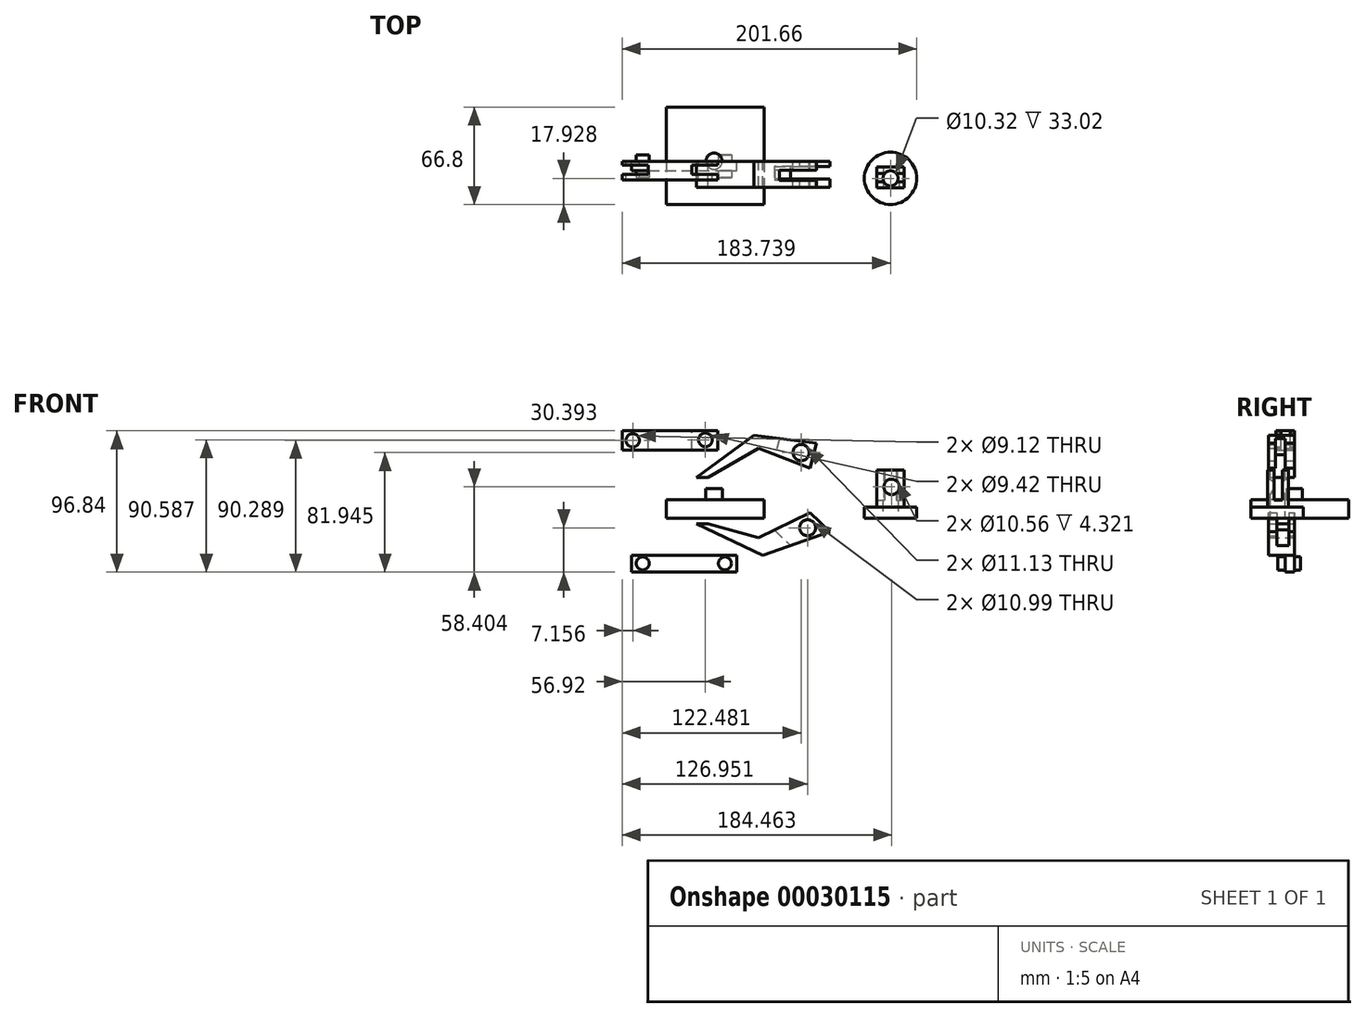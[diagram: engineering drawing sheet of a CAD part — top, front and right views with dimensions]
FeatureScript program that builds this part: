
annotation { "Feature Type Name" : "Feature", "Feature Type Description" : "" }
export const myFeature = defineFeature(function(context is Context, id is Id, definition is map)
    precondition{}
    {
        {
            var Q0;
            Q0=qCreatedBy(makeId("Top.planeOp"),FACE);
            var sketch = newSketch(context, id + "F0", { "sketchPlane" : qUnion([Q0])});
            skLineSegment(sketch, "E0.bottom", {"start": v(-32.78, 37.1) * mm, "end": v(34.27, 37.1) * mm});
            skLineSegment(sketch, "E0.top", {"start": v(-32.78, -29.65) * mm, "end": v(34.27, -29.65) * mm});
            skLineSegment(sketch, "E0.left", {"start": v(-32.78, 37.1) * mm, "end": v(-32.78, -29.65) * mm});
            skLineSegment(sketch, "E0.right", {"start": v(34.27, 37.1) * mm, "end": v(34.27, -29.65) * mm});
            skSolve(sketch);
        }
        {
            var Q0;
            Q0=makeQuery(id+"F0.imprint","IMPRINT",FACE,{"disambiguationData":[TD([[makeQuery(id+"F0.imprint","IMPRINT",EDGE,{"derivedFrom":sQuery(id+"F0.wireOp",EDGE,"E0.bottom")}),-1.0]])]});
            extrude(context, id + "F1", {"entities" : qUnion([Q0]), "depth" : 12.7 * mm});
        }
        {
            var Q0;
            Q0=qCreatedBy(makeId("Front.planeOp"),FACE);
            var sketch = newSketch(context, id + "F2", { "sketchPlane" : qUnion([Q0])});
            skLineSegment(sketch, "E1.bottom", {"start": v(-62.88, 60.04) * mm, "end": v(2.68, 60.04) * mm});
            skLineSegment(sketch, "E1.top", {"start": v(-62.88, 46.93) * mm, "end": v(2.68, 46.93) * mm});
            skLineSegment(sketch, "E1.left", {"start": v(-62.88, 60.04) * mm, "end": v(-62.88, 46.93) * mm});
            skLineSegment(sketch, "E1.right", {"start": v(2.68, 60.04) * mm, "end": v(2.68, 46.93) * mm});
            skCircle(sketch, "E2", {"center": v(-55.72, 53.49) * mm, "radius": 4.56 * mm});
            skCircle(sketch, "E3", {"center": v(-5.96, 53.79) * mm, "radius": 4.71 * mm});
            skSolve(sketch);
        }
        {
            var Q0;
            Q0=makeQuery(id+"F2.imprint","IMPRINT",FACE,{"disambiguationData":[TD([[makeQuery(id+"F2.imprint","IMPRINT",EDGE,{"derivedFrom":sQuery(id+"F2.wireOp",EDGE,"E1.bottom")}),-1.0]])]});
            extrude(context, id + "F3", {"entities" : qUnion([Q0]), "depth" : 12.7 * mm});
        }
        {
            var Q0;
            Q0=makeQuery(id+"F3.opExtrude","SWEPT_FACE",FACE,{"disambiguationData":[OSD([sQuery(id+"F2.wireOp",EDGE,"E1.bottom")])]});
            var sketch = newSketch(context, id + "F4", { "sketchPlane" : qUnion([Q0])});
            skLineSegment(sketch, "E4.bottom", {"start": v(-62.88, -2.83) * mm, "end": v(-45.1, -2.83) * mm});
            skLineSegment(sketch, "E4.top", {"start": v(-62.88, -9.18) * mm, "end": v(-45.1, -9.18) * mm});
            skLineSegment(sketch, "E4.left", {"start": v(-62.88, -2.83) * mm, "end": v(-62.88, -9.18) * mm});
            skLineSegment(sketch, "E4.right", {"start": v(-45.1, -2.83) * mm, "end": v(-45.1, -9.18) * mm});
            skLineSegment(sketch, "E5.bottom", {"start": v(-15.1, -9.18) * mm, "end": v(2.68, -9.18) * mm});
            skLineSegment(sketch, "E5.top", {"start": v(-15.1, -2.83) * mm, "end": v(2.68, -2.83) * mm});
            skLineSegment(sketch, "E5.left", {"start": v(-15.1, -9.18) * mm, "end": v(-15.1, -2.83) * mm});
            skLineSegment(sketch, "E5.right", {"start": v(2.68, -9.18) * mm, "end": v(2.68, -2.83) * mm});
            skSolve(sketch);
        }
        {
            var Q0;
            Q0=makeQuery(id+"F4.imprint","IMPRINT",FACE,{"disambiguationData":[TD([[makeQuery(id+"F4.imprint","IMPRINT",EDGE,{"derivedFrom":sQuery(id+"F4.wireOp",EDGE,"E4.bottom")}),-1.0]])]});
            var Q1;
            Q1=makeQuery(id+"F4.imprint","IMPRINT",FACE,{"disambiguationData":[TD([[makeQuery(id+"F4.imprint","IMPRINT",EDGE,{"derivedFrom":sQuery(id+"F4.wireOp",EDGE,"E5.bottom")}),1.0]])]});
            extrude(context, id + "F5", {"entities" : qUnion([Q0, Q1]), "operationType" : NewBodyOperationType.REMOVE, "oppositeDirection" : true, "depth" : 25.4 * mm});
        }
        {
            var Q0;
            Q0=qCreatedBy(makeId("Front.planeOp"),FACE);
            var sketch = newSketch(context, id + "F6", { "sketchPlane" : qUnion([Q0])});
            skLineSegment(sketch, "E6.bottom", {"start": v(-56.62, -25.18) * mm, "end": v(15.5, -25.18) * mm});
            skLineSegment(sketch, "E6.top", {"start": v(-56.62, -36.8) * mm, "end": v(15.5, -36.8) * mm});
            skLineSegment(sketch, "E6.left", {"start": v(-56.62, -25.18) * mm, "end": v(-56.62, -36.8) * mm});
            skLineSegment(sketch, "E6.right", {"start": v(15.5, -25.18) * mm, "end": v(15.5, -36.8) * mm});
            skSolve(sketch);
        }
        {
            var Q0;
            Q0=makeQuery(id+"F6.imprint","IMPRINT",FACE,{"disambiguationData":[TD([[makeQuery(id+"F6.imprint","IMPRINT",EDGE,{"derivedFrom":sQuery(id+"F6.wireOp",EDGE,"E6.bottom")}),-1.0]])]});
            extrude(context, id + "F7", {"entities" : qUnion([Q0]), "depth" : 6.35 * mm});
        }
        {
            var Q0;
            Q0=makeQuery(id+"F7.opExtrude","CAP_FACE",FACE,{"disambiguationData":[OSD([sQuery(id+"F6.wireOp",EDGE,"E6.bottom"),sQuery(id+"F6.wireOp",EDGE,"E6.top"),sQuery(id+"F6.wireOp",EDGE,"E6.left"),sQuery(id+"F6.wireOp",EDGE,"E6.right")])],"isStart":false});
            var sketch = newSketch(context, id + "F8", { "sketchPlane" : qUnion([Q0])});
            skCircle(sketch, "E7", {"center": v(-48.87, -30.84) * mm, "radius": 4.47 * mm});
            skCircle(sketch, "E8", {"center": v(7.45, -30.84) * mm, "radius": 4.48 * mm});
            skSolve(sketch);
        }
        {
            var Q0;
            Q0=makeQuery(id+"F8.imprint","IMPRINT",FACE,{"disambiguationData":[TD([[makeQuery(id+"F8.imprint","IMPRINT",EDGE,{"derivedFrom":sQuery(id+"F8.wireOp",EDGE,"E7")}),1.0]])]});
            var Q1;
            Q1=makeQuery(id+"F8.imprint","IMPRINT",FACE,{"disambiguationData":[TD([[makeQuery(id+"F8.imprint","IMPRINT",EDGE,{"derivedFrom":sQuery(id+"F8.wireOp",EDGE,"E8")}),1.0]])]});
            extrude(context, id + "F9", {"entities" : qUnion([Q0, Q1]), "operationType" : NewBodyOperationType.ADD, "endBound" : BoundingType.SYMMETRIC, "oppositeDirection" : true, "depth" : 36.23 * mm});
        }
        {
            var Q0;
            Q0=makeQuery(id+"F1.opExtrude","CAP_FACE",FACE,{"disambiguationData":[OSD([sQuery(id+"F0.wireOp",EDGE,"E0.bottom"),sQuery(id+"F0.wireOp",EDGE,"E0.top"),sQuery(id+"F0.wireOp",EDGE,"E0.left"),sQuery(id+"F0.wireOp",EDGE,"E0.right")])],"isStart":false});
            var sketch = newSketch(context, id + "F10", { "sketchPlane" : qUnion([Q0])});
            skCircle(sketch, "E9", {"center": v(0, 0) * mm, "radius": 5.58 * mm});
            skSolve(sketch);
        }
        {
            var Q0;
            Q0=makeQuery(id+"F10.imprint","IMPRINT",FACE,{"disambiguationData":[TD([[makeQuery(id+"F10.imprint","IMPRINT",EDGE,{"derivedFrom":sQuery(id+"F10.wireOp",EDGE,"E9")}),1.0]])]});
            extrude(context, id + "F11", {"entities" : qUnion([Q0]), "operationType" : NewBodyOperationType.ADD, "depth" : 7.62 * mm});
        }
        {
            var Q0;
            Q0=qCreatedBy(makeId("Top.planeOp"),FACE);
            var sketch = newSketch(context, id + "F12", { "sketchPlane" : qUnion([Q0])});
            skCircle(sketch, "E10", {"center": v(120.86, -11.77) * mm, "radius": 17.93 * mm});
            skCircle(sketch, "E11", {"center": v(120.86, -11.77) * mm, "radius": 5.16 * mm});
            skSolve(sketch);
        }
        {
            var Q0;
            Q0=makeQuery(id+"F12.imprint","IMPRINT",FACE,{"disambiguationData":[TD([[makeQuery(id+"F12.imprint","IMPRINT",EDGE,{"derivedFrom":sQuery(id+"F12.wireOp",EDGE,"E10")}),1.0]])]});
            extrude(context, id + "F13", {"entities" : qUnion([Q0]), "depth" : 7.62 * mm});
        }
        {
            var Q0;
            Q0=makeQuery(id+"F13.opExtrude","CAP_FACE",FACE,{"disambiguationData":[OSD([sQuery(id+"F12.wireOp",EDGE,"E10"),sQuery(id+"F12.wireOp",EDGE,"E11")])],"isStart":false});
            var sketch = newSketch(context, id + "F14", { "sketchPlane" : qUnion([Q0])});
            skLineSegment(sketch, "E12.bottom", {"start": v(111.45, -4.02) * mm, "end": v(130.22, -4.02) * mm});
            skLineSegment(sketch, "E12.top", {"start": v(111.45, -18.33) * mm, "end": v(130.22, -18.33) * mm});
            skLineSegment(sketch, "E12.left", {"start": v(111.45, -4.02) * mm, "end": v(111.45, -18.33) * mm});
            skLineSegment(sketch, "E12.right", {"start": v(130.22, -4.02) * mm, "end": v(130.22, -18.33) * mm});
            skSolve(sketch);
        }
        {
            var Q0;
            Q0=makeQuery(id+"F14.imprint","IMPRINT",FACE,{"disambiguationData":[TD([[makeQuery(id+"F14.imprint","IMPRINT",EDGE,{"derivedFrom":sQuery(id+"F14.wireOp",EDGE,"E12.bottom")}),-1.0]])]});
            extrude(context, id + "F15", {"entities" : qUnion([Q0]), "operationType" : NewBodyOperationType.ADD, "depth" : 25.4 * mm});
        }
        {
            var Q0;
            Q0=makeQuery(id+"F15.opExtrude","SWEPT_FACE",FACE,{"disambiguationData":[OSD([sQuery(id+"F14.wireOp",EDGE,"E12.right")])]});
            var sketch = newSketch(context, id + "F16", { "sketchPlane" : qUnion([Q0])});
            skLineSegment(sketch, "E13.bottom", {"start": v(-14, 33.02) * mm, "end": v(-8.34, 33.02) * mm});
            skLineSegment(sketch, "E13.top", {"start": v(-14, 12.37) * mm, "end": v(-8.34, 12.37) * mm});
            skLineSegment(sketch, "E13.left", {"start": v(-14, 33.02) * mm, "end": v(-14, 12.37) * mm});
            skLineSegment(sketch, "E13.right", {"start": v(-8.34, 33.02) * mm, "end": v(-8.34, 12.37) * mm});
            skSolve(sketch);
        }
        {
            var Q0;
            Q0=makeQuery(id+"F16.imprint","IMPRINT",FACE,{"disambiguationData":[TD([[makeQuery(id+"F16.imprint","IMPRINT",EDGE,{"derivedFrom":sQuery(id+"F16.wireOp",EDGE,"E13.bottom")}),1.0]])]});
            extrude(context, id + "F17", {"entities" : qUnion([Q0]), "operationType" : NewBodyOperationType.REMOVE, "oppositeDirection" : true, "depth" : 25.4 * mm});
        }
        {
            var Q0;
            Q0=makeQuery(id+"F15.opExtrude","SWEPT_FACE",FACE,{"disambiguationData":[OSD([sQuery(id+"F14.wireOp",EDGE,"E12.bottom")])]});
            var sketch = newSketch(context, id + "F18", { "sketchPlane" : qUnion([Q0])});
            skCircle(sketch, "E14", {"center": v(-121.58, 21.6) * mm, "radius": 5.28 * mm});
            skSolve(sketch);
        }
        {
            var Q0;
            Q0=makeQuery(id+"F18.imprint","IMPRINT",FACE,{"disambiguationData":[TD([[makeQuery(id+"F18.imprint","IMPRINT",EDGE,{"derivedFrom":sQuery(id+"F18.wireOp",EDGE,"E14")}),1.0]])]});
            extrude(context, id + "F19", {"entities" : qUnion([Q0]), "operationType" : NewBodyOperationType.REMOVE, "oppositeDirection" : true, "depth" : 25.4 * mm});
        }
        {
            var Q0;
            Q0=makeQuery(id+"F9.opExtrude","CAP_FACE",FACE,{"disambiguationData":[OSD([sQuery(id+"F8.wireOp",EDGE,"E8")])],"isStart":false});
            extrude(context, id + "F20", {"entities" : qUnion([Q0]), "operationType" : NewBodyOperationType.REMOVE, "oppositeDirection" : true, "depth" : 7.62 * mm});
        }
        {
            var Q0;
            Q0=makeQuery(id+"F9.opExtrude","CAP_FACE",FACE,{"disambiguationData":[OSD([sQuery(id+"F8.wireOp",EDGE,"E8")])],"isStart":true});
            extrude(context, id + "F21", {"entities" : qUnion([Q0]), "operationType" : NewBodyOperationType.REMOVE, "depth" : 17.78 * mm});
        }
        {
            var Q0;
            Q0=makeQuery(id+"F9.opExtrude","CAP_FACE",FACE,{"disambiguationData":[OSD([sQuery(id+"F8.wireOp",EDGE,"E8")])],"isStart":true});
            extrude(context, id + "F22", {"entities" : qUnion([Q0]), "operationType" : NewBodyOperationType.REMOVE, "oppositeDirection" : true, "depth" : 13.2 * mm});
        }
        {
            var Q0;
            Q0=makeQuery(id+"F9.opExtrude","CAP_FACE",FACE,{"disambiguationData":[OSD([sQuery(id+"F8.wireOp",EDGE,"E7")])],"isStart":true});
            extrude(context, id + "F23", {"entities" : qUnion([Q0]), "operationType" : NewBodyOperationType.REMOVE, "oppositeDirection" : true, "depth" : 13.2 * mm});
        }
        {
            var Q0;
            Q0=makeQuery(id+"F9.opExtrude","CAP_FACE",FACE,{"disambiguationData":[OSD([sQuery(id+"F8.wireOp",EDGE,"E7")])],"isStart":false});
            extrude(context, id + "F24", {"entities" : qUnion([Q0]), "operationType" : NewBodyOperationType.REMOVE, "oppositeDirection" : true, "depth" : 7.62 * mm});
        }
        {
            var Q0;
            Q0=qCreatedBy(makeId("Front.planeOp"),FACE);
            var sketch = newSketch(context, id + "F25", { "sketchPlane" : qUnion([Q0])});
            skLineSegment(sketch, "E15", {"start": v(70.03, 51.4) * mm, "end": v(65.56, 34.42) * mm});
            skLineSegment(sketch, "E16", {"start": v(65.56, 34.42) * mm, "end": v(30.4, 48.13) * mm});
            skLineSegment(sketch, "E17", {"start": v(30.4, 48.13) * mm, "end": v(-4.17, 28.16) * mm});
            skLineSegment(sketch, "E18", {"start": v(-4.17, 28.16) * mm, "end": v(-11.92, 28.16) * mm});
            skLineSegment(sketch, "E19", {"start": v(-11.92, 28.16) * mm, "end": v(27.42, 57.06) * mm});
            skLineSegment(sketch, "E20", {"start": v(27.42, 57.06) * mm, "end": v(70.03, 51.4) * mm});
            skLineSegment(sketch, "E21", {"start": v(65.56, 4.02) * mm, "end": v(30.4, -13.26) * mm});
            skLineSegment(sketch, "E22", {"start": v(30.4, -13.26) * mm, "end": v(-4.17, -3.72) * mm});
            skLineSegment(sketch, "E23", {"start": v(-4.17, -3.72) * mm, "end": v(-11.92, -3.72) * mm});
            skLineSegment(sketch, "E24", {"start": v(-11.92, -3.72) * mm, "end": v(33.38, -25.18) * mm});
            skLineSegment(sketch, "E25", {"start": v(33.38, -25.18) * mm, "end": v(79.27, -9.09) * mm});
            skLineSegment(sketch, "E26", {"start": v(79.27, -9.09) * mm, "end": v(65.56, 4.02) * mm});
            skCircle(sketch, "E27", {"center": v(64.07, -6.4) * mm, "radius": 5.5 * mm});
            skCircle(sketch, "E28", {"center": v(59.6, 45.15) * mm, "radius": 5.57 * mm});
            skSolve(sketch);
        }
        {
            var Q0;
            Q0=makeQuery(id+"F25.imprint","IMPRINT",FACE,{"disambiguationData":[TD([[makeQuery(id+"F25.imprint","IMPRINT",EDGE,{"derivedFrom":sQuery(id+"F25.wireOp",EDGE,"E15")}),-1.0]])]});
            var Q1;
            Q1=makeQuery(id+"F25.imprint","IMPRINT",FACE,{"disambiguationData":[TD([[makeQuery(id+"F25.imprint","IMPRINT",EDGE,{"derivedFrom":sQuery(id+"F25.wireOp",EDGE,"E21")}),1.0]])]});
            extrude(context, id + "F26", {"entities" : qUnion([Q0, Q1]), "depth" : 17.78 * mm});
        }
        {
            var Q0;
            Q0=makeQuery(id+"F26.opExtrude","SWEPT_FACE",FACE,{"disambiguationData":[OSD([sQuery(id+"F25.wireOp",EDGE,"E15")])]});
            var sketch = newSketch(context, id + "F27", { "sketchPlane" : qUnion([Q0])});
            skLineSegment(sketch, "E29.bottom", {"start": v(-13.11, 77.7) * mm, "end": v(-6.26, 77.7) * mm});
            skLineSegment(sketch, "E29.top", {"start": v(-13.11, 45.66) * mm, "end": v(-6.26, 45.66) * mm});
            skLineSegment(sketch, "E29.left", {"start": v(-13.11, 77.7) * mm, "end": v(-13.11, 45.66) * mm});
            skLineSegment(sketch, "E29.right", {"start": v(-6.26, 77.7) * mm, "end": v(-6.26, 45.66) * mm});
            skLineSegment(sketch, "E30.bottom", {"start": v(-12.81, 19.77) * mm, "end": v(-6.26, 19.77) * mm});
            skLineSegment(sketch, "E30.top", {"start": v(-12.81, -12.27) * mm, "end": v(-6.26, -12.27) * mm});
            skLineSegment(sketch, "E30.left", {"start": v(-12.81, 19.77) * mm, "end": v(-12.81, -12.27) * mm});
            skLineSegment(sketch, "E30.right", {"start": v(-6.26, 19.77) * mm, "end": v(-6.26, -12.27) * mm});
            skSolve(sketch);
        }
        {
            var Q0;
            {var subQ5=sQuery(id+"F27.wireOp",EDGE,"E29.bottom");Q0=makeQuery(id+"F27.imprint","IMPRINT",FACE,{"disambiguationData":[TD([[makeQuery(id+"F27.imprint","IMPRINT",EDGE,{"derivedFrom":subQ5}),-1.0]])]});}
            var Q1;
            {var subQ0=sQuery(id+"F25.wireOp",EDGE,"E15");var subQ4=sQuery(id+"F27.wireOp",EDGE,"E29.left");var subQ6=makeQuery(id+"F26.opExtrude","SWEPT_EDGE",EDGE,{"disambiguationData":[OSD([subQ0,sQuery(id+"F25.wireOp",EDGE,"E20")])]});var subQ8=makeQuery(id+"F27.imprint","INTERSECT",VERTEX,{"derivedFrom":[subQ6,subQ4]});Q1=makeQuery(id+"F27.imprint","IMPRINT",FACE,{"disambiguationData":[TD([[makeQuery(id+"F27.imprint","IMPRINT",EDGE,{"disambiguationData":[TD([[subQ8,-1.0]])],"derivedFrom":subQ4}),1.0]])]});}
            var Q2;
            {var subQ3=sQuery(id+"F27.wireOp",EDGE,"E29.top");Q2=makeQuery(id+"F27.imprint","IMPRINT",FACE,{"disambiguationData":[TD([[makeQuery(id+"F27.imprint","IMPRINT",EDGE,{"derivedFrom":subQ3}),1.0]])]});}
            extrude(context, id + "F28", {"entities" : qUnion([Q0, Q1, Q2]), "operationType" : NewBodyOperationType.REMOVE, "oppositeDirection" : true, "depth" : 25.4 * mm});
        }
        {
            var Q0;
            Q0=makeQuery(id+"F26.opExtrude","SWEPT_FACE",FACE,{"disambiguationData":[OSD([sQuery(id+"F25.wireOp",EDGE,"E26")])]});
            var sketch = newSketch(context, id + "F29", { "sketchPlane" : qUnion([Q0])});
            skLineSegment(sketch, "E31.bottom", {"start": v(35.11, -3.72) * mm, "end": v(73.46, -3.72) * mm});
            skLineSegment(sketch, "E31.top", {"start": v(35.11, -12.07) * mm, "end": v(73.46, -12.07) * mm});
            skLineSegment(sketch, "E31.left", {"start": v(35.11, -3.72) * mm, "end": v(35.11, -12.07) * mm});
            skLineSegment(sketch, "E31.right", {"start": v(73.46, -3.72) * mm, "end": v(73.46, -12.07) * mm});
            skSolve(sketch);
        }
        {
            var Q0;
            {var subQ0=sQuery(id+"F25.wireOp",EDGE,"E26");var subQ4=sQuery(id+"F29.wireOp",EDGE,"E31.bottom");var subQ6=makeQuery(id+"F26.opExtrude","SWEPT_EDGE",EDGE,{"disambiguationData":[OSD([sQuery(id+"F25.wireOp",EDGE,"E21"),subQ0])]});var subQ8=makeQuery(id+"F29.imprint","INTERSECT",VERTEX,{"derivedFrom":[subQ6,subQ4]});Q0=makeQuery(id+"F29.imprint","IMPRINT",FACE,{"disambiguationData":[TD([[makeQuery(id+"F29.imprint","IMPRINT",EDGE,{"disambiguationData":[TD([[subQ8,-1.0]])],"derivedFrom":subQ4}),-1.0]])]});}
            var Q1;
            {var subQ5=sQuery(id+"F29.wireOp",EDGE,"E31.left");Q1=makeQuery(id+"F29.imprint","IMPRINT",FACE,{"disambiguationData":[TD([[makeQuery(id+"F29.imprint","IMPRINT",EDGE,{"derivedFrom":subQ5}),1.0]])]});}
            var Q2;
            {var subQ5=sQuery(id+"F29.wireOp",EDGE,"E31.right");Q2=makeQuery(id+"F29.imprint","IMPRINT",FACE,{"disambiguationData":[TD([[makeQuery(id+"F29.imprint","IMPRINT",EDGE,{"derivedFrom":subQ5}),-1.0]])]});}
            extrude(context, id + "F30", {"entities" : qUnion([Q0, Q1, Q2]), "operationType" : NewBodyOperationType.REMOVE, "oppositeDirection" : true, "depth" : 25.4 * mm});
        }
    });
